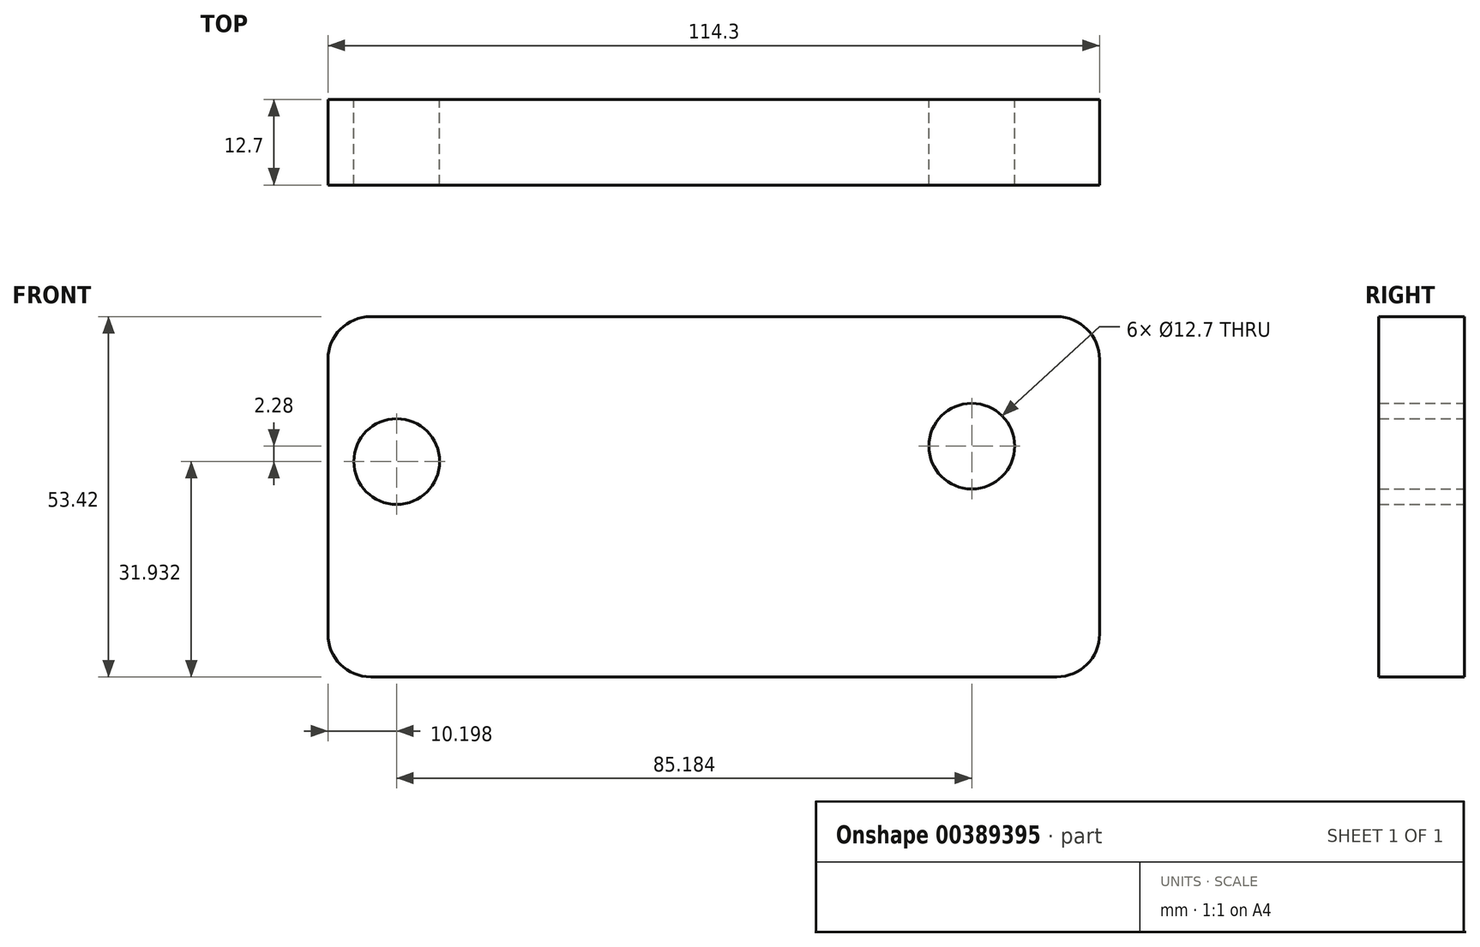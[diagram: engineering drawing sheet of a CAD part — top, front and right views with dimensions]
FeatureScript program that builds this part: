
annotation { "Feature Type Name" : "Feature", "Feature Type Description" : "" }
export const myFeature = defineFeature(function(context is Context, id is Id, definition is map)
    precondition{}
    {
        {
            var Q0;
            Q0=qCreatedBy(makeId("Front.planeOp"),FACE);
            var sketch = newSketch(context, id + "F0", { "sketchPlane" : qUnion([Q0])});
            skLineSegment(sketch, "E0.bottom", {"start": v(-46.08, 27.8) * mm, "end": v(55.52, 27.8) * mm});
            skLineSegment(sketch, "E0.top", {"start": v(-46.08, -25.62) * mm, "end": v(55.52, -25.62) * mm});
            skLineSegment(sketch, "E0.left", {"start": v(-52.43, 21.45) * mm, "end": v(-52.43, -19.27) * mm});
            skLineSegment(sketch, "E0.right", {"start": v(61.87, 21.45) * mm, "end": v(61.87, -19.27) * mm});
            skCircle(sketch, "E1", {"center": v(-42.23, 6.31) * mm, "radius": 6.35 * mm});
            skCircle(sketch, "E2", {"center": v(42.95, 8.6) * mm, "radius": 6.35 * mm});
            skPoint(sketch, "E3.visualSharp", {"position": v(-52.43, 27.8) * mm});
            skArc(sketch, "E3.filletArc", {"start": v(-46.08, 27.8) * mm, "mid": v(-50.57, 25.94) * mm, "end": v(-52.43, 21.45) * mm});
            skPoint(sketch, "E4.visualSharp", {"position": v(61.87, 27.8) * mm});
            skArc(sketch, "E4.filletArc", {"start": v(61.87, 21.45) * mm, "mid": v(60.01, 25.94) * mm, "end": v(55.52, 27.8) * mm});
            skPoint(sketch, "E5.visualSharp", {"position": v(-52.43, -25.62) * mm});
            skArc(sketch, "E5.filletArc", {"start": v(-52.43, -19.27) * mm, "mid": v(-50.57, -23.76) * mm, "end": v(-46.08, -25.62) * mm});
            skPoint(sketch, "E6.visualSharp", {"position": v(61.87, -25.62) * mm});
            skArc(sketch, "E6.filletArc", {"start": v(55.52, -25.62) * mm, "mid": v(60.01, -23.76) * mm, "end": v(61.87, -19.27) * mm});
            skSolve(sketch);
        }
        {
            var Q0;
            Q0 = qSketchRegion(id + "F0", true);
            extrude(context, id + "F1", {"entities" : qUnion([Q0]), "depth" : 12.7 * mm});
        }
    });
